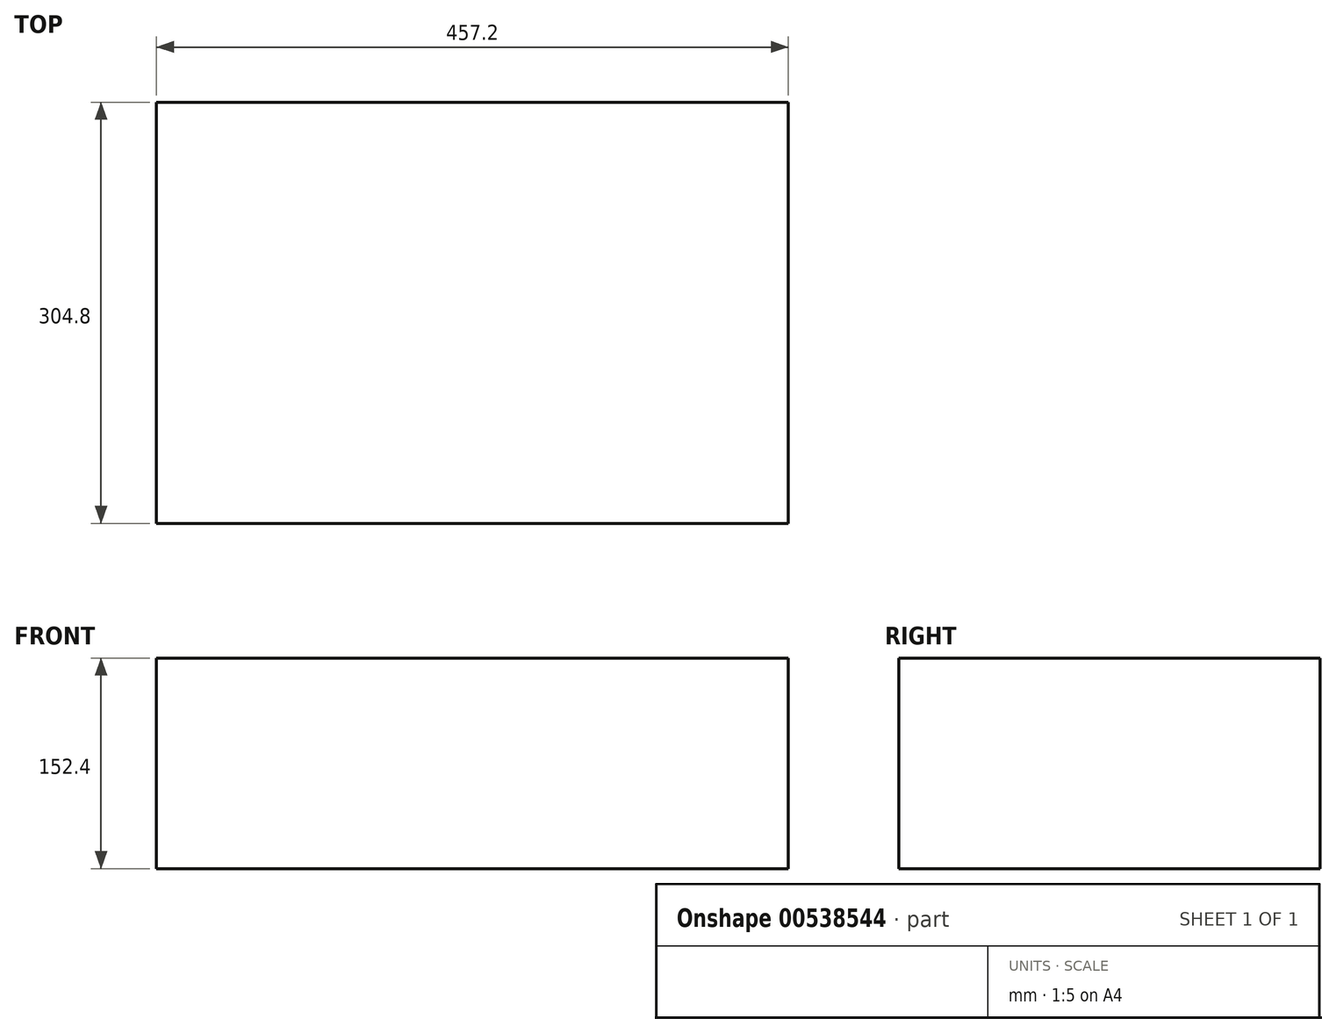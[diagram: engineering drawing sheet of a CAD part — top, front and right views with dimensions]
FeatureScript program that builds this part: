
annotation { "Feature Type Name" : "Feature", "Feature Type Description" : "" }
export const myFeature = defineFeature(function(context is Context, id is Id, definition is map)
    precondition{}
    {
        {
            var Q0;
            Q0=qCreatedBy(makeId("Front.planeOp"),FACE);
            var sketch = newSketch(context, id + "F0", { "sketchPlane" : qUnion([Q0])});
            skLineSegment(sketch, "E0.bottom", {"start": v(-228.6, 60.96) * mm, "end": v(228.6, 60.96) * mm});
            skLineSegment(sketch, "E0.top", {"start": v(-228.6, -91.44) * mm, "end": v(228.6, -91.44) * mm});
            skLineSegment(sketch, "E0.left", {"start": v(-228.6, 60.96) * mm, "end": v(-228.6, -91.44) * mm});
            skLineSegment(sketch, "E0.right", {"start": v(228.6, 60.96) * mm, "end": v(228.6, -91.44) * mm});
            skPoint(sketch, "E0.middle", {"position": v(0, -15.24) * mm});
            skSolve(sketch);
        }
        {
            var Q0;
            Q0 = qSketchRegion(id + "F0", true);
            extrude(context, id + "F1", {"entities" : qUnion([Q0]), "depth" : 304.8 * mm, "offsetDistance" : 25.4 * mm});
        }
    });
